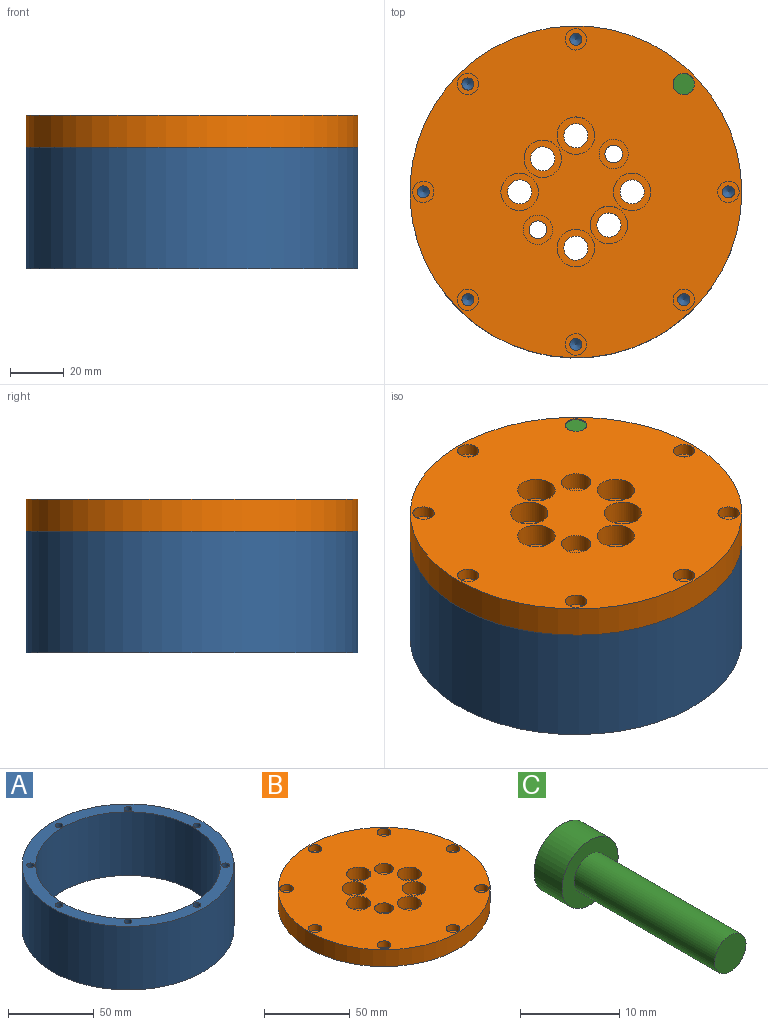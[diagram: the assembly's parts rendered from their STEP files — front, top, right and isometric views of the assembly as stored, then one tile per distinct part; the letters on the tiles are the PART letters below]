
ASSEMBLY  parts=3 mates=2
PART A: 20 faces, bbox 124x124x45.5 mm
  f0: cylinder r=54mm len=108mm, axis (0,0,1), area 15437.8mm2, adj f2,f3
  f1: cylinder r=62mm len=124mm, axis (0,0,1), area 17724.9mm2, adj f2,f3
  f2: plane 124x124mm, normal (0,0,-1), area 2915.4mm2, adj f0,f1
  f3: plane 124x124mm, normal (0,0,1), area 2788.2mm2, adj f0,f1,f5,f7,f9,f11,f13,f15
  f4: cone r=0mm half-angle=59deg, axis (0,0,1), area 18.6mm2, adj f5
  f5: cylinder r=2.25mm len=10mm, axis (0,0,1), area 141.4mm2, adj f3,f4
  f6: cone r=0mm half-angle=59deg, axis (0,0,1), area 18.6mm2, adj f7
  f7: cylinder r=2.25mm len=10mm, axis (0,0,1), area 141.4mm2, adj f3,f6
  f8: cone r=0mm half-angle=59deg, axis (0,0,1), area 18.6mm2, adj f9
  f9: cylinder r=2.25mm len=10mm, axis (0,0,1), area 141.4mm2, adj f3,f8
  f10: cone r=0mm half-angle=59deg, axis (0,0,1), area 18.6mm2, adj f11
  f11: cylinder r=2.25mm len=10mm, axis (0,0,1), area 141.4mm2, adj f3,f10
  f12: cone r=0mm half-angle=59deg, axis (0,0,1), area 18.6mm2, adj f13
  f13: cylinder r=2.25mm len=10mm, axis (0,0,1), area 141.4mm2, adj f3,f12
  f14: cone r=0mm half-angle=59deg, axis (0,0,1), area 18.6mm2, adj f15
  f15: cylinder r=2.25mm len=10mm, axis (0,0,1), area 141.4mm2, adj f3,f14
  f16: cone r=0mm half-angle=59deg, axis (0,0,1), area 18.6mm2, adj f17
  f17: cylinder r=2.25mm len=10mm, axis (0,0,1), area 141.4mm2, adj f3,f16
  f18: cone r=0mm half-angle=59deg, axis (0,0,1), area 18.6mm2, adj f19
  f19: cylinder r=2.25mm len=10mm, axis (0,0,1), area 141.4mm2, adj f3,f18
PART B: 51 faces, bbox 124x124x12 mm
  f0: cylinder r=62mm len=124mm, axis (0,0,-1), area 4674.7mm2, adj f1,f2
  f1: plane 124x124mm, normal (0,0,1), area 10560.5mm2, adj f0,f5,f8,f11,f14,f17,f20,f23
  f2: plane 124x124mm, normal (0,0,-1), area 11498.9mm2, adj f0,f3,f6,f9,f12,f15,f18,f21
  f3: cylinder r=2.25mm len=7.6mm, axis (0,0,1), area 107.4mm2, adj f2,f4
  f4: plane 8x8mm, normal (0,0,1), area 34.4mm2, adj f3,f5
  f5: cylinder r=4mm len=8mm, axis (0,0,1), area 110.6mm2, adj f1,f4
  f6: cylinder r=2.25mm len=7.6mm, axis (0,0,1), area 107.4mm2, adj f2,f7
  f7: plane 8x8mm, normal (0,0,1), area 34.4mm2, adj f6,f8
  f8: cylinder r=4mm len=8mm, axis (0,0,1), area 110.6mm2, adj f1,f7
  f9: cylinder r=2.25mm len=7.6mm, axis (0,0,1), area 107.4mm2, adj f2,f10
  f10: plane 8x8mm, normal (0,0,1), area 34.4mm2, adj f9,f11
  f11: cylinder r=4mm len=8mm, axis (0,0,1), area 110.6mm2, adj f1,f10
  f12: cylinder r=2.25mm len=7.6mm, axis (0,0,1), area 107.4mm2, adj f2,f13
  f13: plane 8x8mm, normal (0,0,1), area 34.4mm2, adj f12,f14
  f14: cylinder r=4mm len=8mm, axis (0,0,1), area 110.6mm2, adj f1,f13
  f15: cylinder r=2.25mm len=7.6mm, axis (0,0,1), area 107.4mm2, adj f2,f16
  f16: plane 8x8mm, normal (0,0,1), area 34.4mm2, adj f15,f17
  f17: cylinder r=4mm len=8mm, axis (0,0,1), area 110.6mm2, adj f1,f16
  f18: cylinder r=2.25mm len=7.6mm, axis (0,0,1), area 107.4mm2, adj f2,f19
  f19: plane 8x8mm, normal (0,0,1), area 34.4mm2, adj f18,f20
  f20: cylinder r=4mm len=8mm, axis (0,0,1), area 110.6mm2, adj f1,f19
  f21: cylinder r=2.25mm len=7.6mm, axis (0,0,1), area 107.4mm2, adj f2,f22
  f22: plane 8x8mm, normal (0,0,1), area 34.4mm2, adj f21,f23
  f23: cylinder r=4mm len=8mm, axis (0,0,1), area 110.6mm2, adj f1,f22
  f24: cylinder r=2.25mm len=7.6mm, axis (0,0,1), area 107.4mm2, adj f2,f25
  f25: plane 8x8mm, normal (0,0,1), area 34.4mm2, adj f24,f26
  f26: cylinder r=4mm len=8mm, axis (0,0,1), area 110.6mm2, adj f1,f25
  f27: cylinder r=4.5mm len=9mm, axis (0,0,1), area 90.5mm2, adj f2,f28
  f28: plane 14x14mm, normal (0,0,1), area 90.3mm2, adj f27,f29
  f29: cylinder r=7mm len=14mm, axis (0,0,1), area 387mm2, adj f1,f28
  f30: cylinder r=4.5mm len=9mm, axis (0,0,1), area 90.5mm2, adj f2,f31
  f31: plane 14x14mm, normal (0,0,1), area 90.3mm2, adj f30,f32
  f32: cylinder r=7mm len=14mm, axis (0,0,1), area 387mm2, adj f1,f31
  f33: cylinder r=4.5mm len=9mm, axis (0,0,1), area 90.5mm2, adj f2,f34
  f34: plane 14x14mm, normal (0,0,1), area 90.3mm2, adj f33,f35
  f35: cylinder r=7mm len=14mm, axis (0,0,1), area 387mm2, adj f1,f34
  f36: cylinder r=4.5mm len=9mm, axis (0,0,1), area 90.5mm2, adj f2,f37
  f37: plane 14x14mm, normal (0,0,1), area 90.3mm2, adj f36,f38
  f38: cylinder r=7mm len=14mm, axis (0,0,1), area 387mm2, adj f1,f37
  f39: cylinder r=4.5mm len=9mm, axis (0,0,1), area 90.5mm2, adj f2,f40
  f40: plane 14x14mm, normal (0,0,1), area 90.3mm2, adj f39,f41
  f41: cylinder r=7mm len=14mm, axis (0,0,1), area 387mm2, adj f1,f40
  f42: cylinder r=4.5mm len=9mm, axis (0,0,1), area 90.5mm2, adj f2,f43
  f43: plane 14x14mm, normal (0,0,1), area 90.3mm2, adj f42,f44
  f44: cylinder r=7mm len=14mm, axis (0,0,1), area 387mm2, adj f1,f43
  f45: cylinder r=3.3mm len=6.6mm, axis (0,0,1), area 112mm2, adj f2,f46
  f46: plane 11x11mm, normal (0,0,1), area 60.8mm2, adj f45,f47
  f47: cylinder r=5.5mm len=11mm, axis (0,0,1), area 228.1mm2, adj f1,f46
  f48: cylinder r=3.3mm len=6.6mm, axis (0,0,1), area 112mm2, adj f2,f49
  f49: plane 11x11mm, normal (0,0,1), area 60.8mm2, adj f48,f50
  f50: cylinder r=5.5mm len=11mm, axis (0,0,1), area 228.1mm2, adj f1,f49
PART C: 5 faces, bbox 8x24x8 mm
  f0: plane 4.5x4.5mm, normal (0,-1,0), area 15.9mm2, adj f4
  f1: plane 8x8mm, normal (0,1,0), area 50.3mm2, adj f2
  f2: cylinder r=4mm len=8mm, axis (0,-1,0), area 100.5mm2, adj f1,f3
  f3: plane 8x8mm, normal (0,-1,0), area 34.4mm2, adj f2,f4
  f4: cylinder r=2.25mm len=20mm, axis (0,-1,0), area 282.7mm2, adj f0,f3
PLACE A at identity
PLACE B at identity
PLACE C rot(axis=(1,0,0),90deg) t=(40.31,40.31,16.74)mm
MATE fastened C.f2 <-> B.f21  axis (0,0,-1) through (40.31,40.31,7.6)mm
MATE fastened B.f24 <-> A.f18  axis (0,0,-1) through (0,57,0)mm
